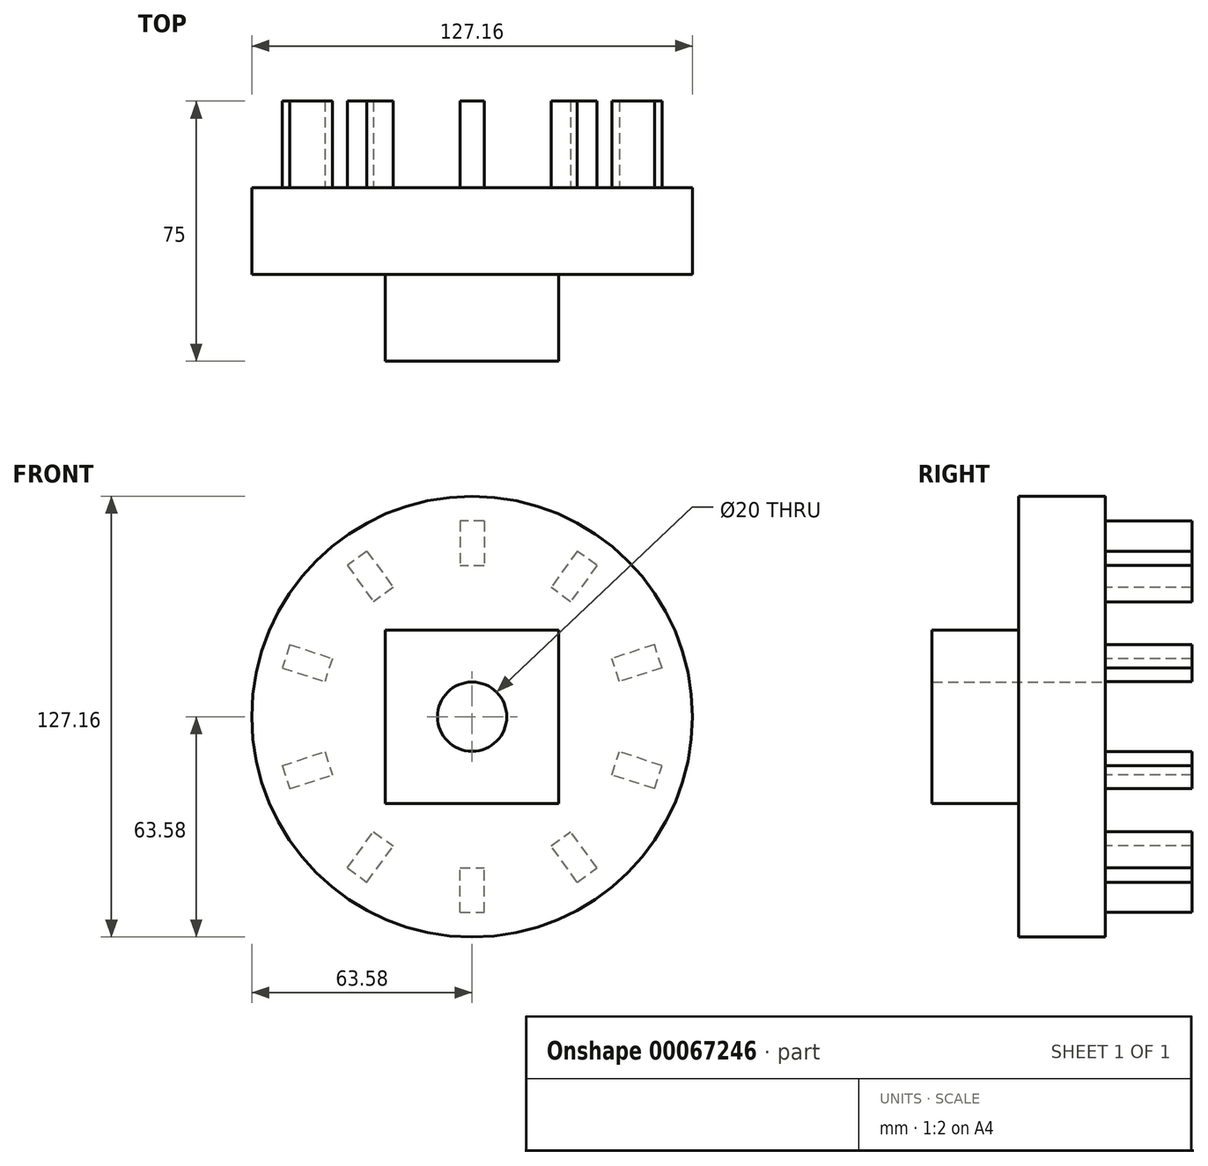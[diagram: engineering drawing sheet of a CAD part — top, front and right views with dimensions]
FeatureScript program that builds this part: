
annotation { "Feature Type Name" : "Feature", "Feature Type Description" : "" }
export const myFeature = defineFeature(function(context is Context, id is Id, definition is map)
    precondition{}
    {
        {
            var Q0;
            Q0=qCreatedBy(makeId("Front.planeOp"),FACE);
            var sketch = newSketch(context, id + "F0", { "sketchPlane" : qUnion([Q0])});
            skCircle(sketch, "E0", {"center": v(0, 0) * mm, "radius": 63.58 * mm});
            skSolve(sketch);
        }
        {
            var Q0;
            Q0=makeQuery(id+"F0.imprint","IMPRINT",FACE,{"disambiguationData":[TD([[makeQuery(id+"F0.imprint","IMPRINT",EDGE,{"derivedFrom":sQuery(id+"F0.wireOp",EDGE,"E0")}),1.0]])]});
            extrude(context, id + "F1", {"entities" : qUnion([Q0]), "depth" : 25 * mm});
        }
        {
            var Q0;
            Q0=makeQuery(id+"F1.opExtrude","CAP_FACE",FACE,{"disambiguationData":[OSD([sQuery(id+"F0.wireOp",EDGE,"E0")])],"isStart":true});
            var sketch = newSketch(context, id + "F2", { "sketchPlane" : qUnion([Q0])});
            skCircle(sketch, "E1", {"center": v(0, 0) * mm, "radius": 10 * mm});
            skLineSegment(sketch, "E2.rect.bottom", {"start": v(25, -25) * mm, "end": v(-25, -25) * mm});
            skLineSegment(sketch, "E2.rect.top", {"start": v(25, 25) * mm, "end": v(-25, 25) * mm});
            skLineSegment(sketch, "E2.rect.left", {"start": v(25, -25) * mm, "end": v(25, 25) * mm});
            skLineSegment(sketch, "E2.rect.right", {"start": v(-25, -25) * mm, "end": v(-25, 25) * mm});
            skSolve(sketch);
        }
        {
            var Q0;
            Q0=makeQuery(id+"F2.imprint","IMPRINT",FACE,{"disambiguationData":[TD([[makeQuery(id+"F2.imprint","IMPRINT",EDGE,{"derivedFrom":sQuery(id+"F2.wireOp",EDGE,"E1")}),1.0]])]});
            var Q1;
            Q1=sQuery(id+"F2.wireOp",EDGE,"E1");
            extrude(context, id + "F3", {"entities" : qUnion([Q0]), "operationType" : NewBodyOperationType.REMOVE, "surfaceEntities" : qUnion([Q1]), "endBound" : BoundingType.THROUGH_ALL, "oppositeDirection" : true, "depth" : 25 * mm});
        }
        {
            var Q0;
            Q0=makeQuery(id+"F1.opExtrude","CAP_FACE",FACE,{"disambiguationData":[OSD([sQuery(id+"F0.wireOp",EDGE,"E0")])],"isStart":false});
            var sketch = newSketch(context, id + "F4", { "sketchPlane" : qUnion([Q0])});
            skLineSegment(sketch, "E3.0", {"start": v(-25, 25) * mm, "end": v(25, 25) * mm});
            skLineSegment(sketch, "E4.0", {"start": v(25, -25) * mm, "end": v(25, 25) * mm});
            skLineSegment(sketch, "E5.0", {"start": v(-25, -25) * mm, "end": v(25, -25) * mm});
            skLineSegment(sketch, "E6.0", {"start": v(-25, -25) * mm, "end": v(-25, 25) * mm});
            skCircle(sketch, "E7.0", {"center": v(0, 0) * mm, "radius": 10 * mm});
            skSolve(sketch);
        }
        {
            var Q0;
            Q0=makeQuery(id+"F4.imprint","IMPRINT",FACE,{"disambiguationData":[TD([[makeQuery(id+"F4.imprint","IMPRINT",EDGE,{"derivedFrom":sQuery(id+"F4.wireOp",EDGE,"E3.0")}),-1.0]])]});
            extrude(context, id + "F5", {"entities" : qUnion([Q0]), "operationType" : NewBodyOperationType.ADD, "depth" : 25 * mm});
        }
        {
            var Q0;
            Q0=makeQuery(id+"F1.opExtrude","CAP_FACE",FACE,{"disambiguationData":[OSD([sQuery(id+"F0.wireOp",EDGE,"E0")])],"isStart":true});
            var sketch = newSketch(context, id + "F6", { "sketchPlane" : qUnion([Q0])});
            skCircle(sketch, "E8", {"center": v(0, 0) * mm, "radius": 50 * mm, "construction": true});
            skLineSegment(sketch, "E9.rect.bottom", {"start": v(3.5, -56.45) * mm, "end": v(-3.5, -56.45) * mm});
            skLineSegment(sketch, "E9.rect.top", {"start": v(3.5, -43.55) * mm, "end": v(-3.5, -43.55) * mm});
            skLineSegment(sketch, "E9.rect.left", {"start": v(3.5, -56.45) * mm, "end": v(3.5, -43.55) * mm});
            skLineSegment(sketch, "E9.rect.right", {"start": v(-3.5, -56.45) * mm, "end": v(-3.5, -43.55) * mm});
            skPoint(sketch, "E9.rect.middle", {"position": v(0, -50) * mm});
            skSolve(sketch);
        }
        {
            var Q0;
            Q0 = qSketchRegion(id + "F6", true);
            extrude(context, id + "F7", {"entities" : qUnion([Q0]), "operationType" : NewBodyOperationType.ADD, "depth" : 25 * mm});
        }
        {
            var Q0;
            Q0=makeQuery(id+"F7.opExtrude","SWEPT_FACE",FACE,{"disambiguationData":[OSD([sQuery(id+"F6.wireOp",EDGE,"E9.rect.left")])]});
            var Q1;
            Q1=makeQuery(id+"F7.opExtrude","CAP_FACE",FACE,{"disambiguationData":[OSD([sQuery(id+"F6.wireOp",EDGE,"E9.rect.bottom"),sQuery(id+"F6.wireOp",EDGE,"E9.rect.top"),sQuery(id+"F6.wireOp",EDGE,"E9.rect.left"),sQuery(id+"F6.wireOp",EDGE,"E9.rect.right")])],"isStart":false});
            var Q2;
            Q2=makeQuery(id+"F7.opExtrude","SWEPT_FACE",FACE,{"disambiguationData":[OSD([sQuery(id+"F6.wireOp",EDGE,"E9.rect.right")])]});
            var Q3;
            Q3=makeQuery(id+"F7.opExtrude","SWEPT_FACE",FACE,{"disambiguationData":[OSD([sQuery(id+"F6.wireOp",EDGE,"E9.rect.top")])]});
            var Q4;
            Q4=makeQuery(id+"F7.opExtrude","SWEPT_FACE",FACE,{"disambiguationData":[OSD([sQuery(id+"F6.wireOp",EDGE,"E9.rect.bottom")])]});
            var Q5;
            Q5=makeQuery(id+"F1.opExtrude","CAP_EDGE",EDGE,{"disambiguationData":[OSD([sQuery(id+"F0.wireOp",EDGE,"E0")])],"isStart":true});
            circularPattern(context, id + "F8", {"faces" : qUnion([Q0, Q1, Q2, Q3, Q4]), "axis" : qUnion([Q5]), "angle" : 360 * degree, "instanceCount" : 10, "equalSpace" : true, "patternType" : PatternType.FACE});
        }
    });
